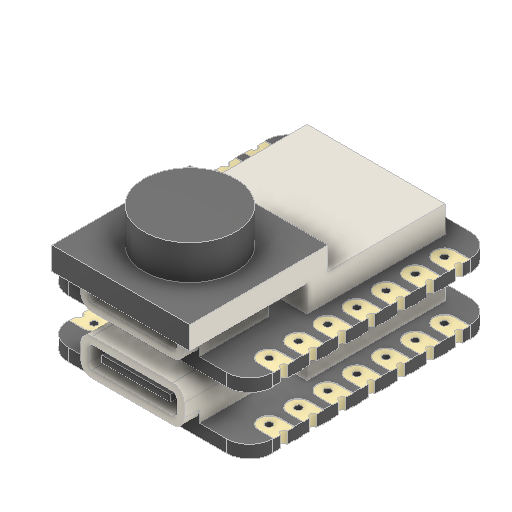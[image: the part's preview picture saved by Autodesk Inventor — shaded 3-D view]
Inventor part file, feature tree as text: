
AUTODESK INVENTOR PART (.ipt)
format: ipt  version: 2022 (Build 260153000, 153)  size: 497,152 bytes
history: native  units: mm
features: extrude x2, sketch x2, projected_geometry x2, pattern_linear x1
ambient origin geometry x8: Origin, YZ Plane, XZ Plane, XY Plane, X Axis, Y Axis, Z Axis, Center Point
bodies: Volumenkörper1 (feature_tree), Body1 (feature_tree)
feature tree (7):
  extrude  "Extrusion1"  Depth=5.0mm TaperAngle=0.0deg
  extrude  "Extrusion2"  Depth=12.0mm
  pattern_linear  "Rechteckige Anordnung1"  Spacing1=2.0mm  [1 undecoded]
  sketch  "Skizze1"  dims[d0=8.0mm d1=5.0mm d2=0.0mm]
  projected_geometry  "Projizierte Kontur1"
  sketch  "Skizze2"  dims[d3=12.0mm d4=12.0mm d5=2.0mm d6=0.0mm d7=20.0mm d9=5.0mm]
  projected_geometry  "Projizierte Kontur2"
note: 1 required parameter value undecoded (feature->parameter linkage not recoverable at this tier; creation-order binding heuristic only, values carry confidence <= 0.55)
